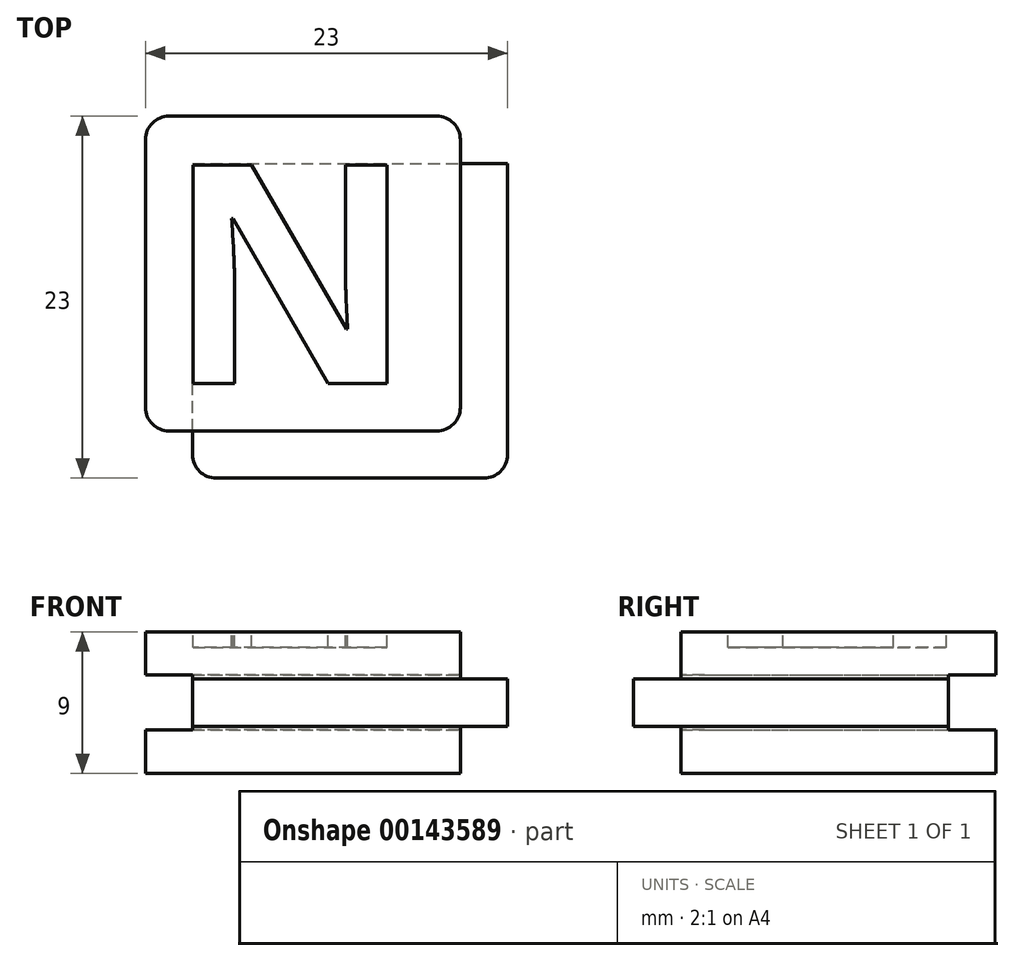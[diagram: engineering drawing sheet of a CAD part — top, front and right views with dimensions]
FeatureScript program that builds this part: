
annotation { "Feature Type Name" : "Feature", "Feature Type Description" : "" }
export const myFeature = defineFeature(function(context is Context, id is Id, definition is map)
    precondition{}
    {
        {
            var Q0;
            Q0=qCreatedBy(makeId("Front.planeOp"),FACE);
            var sketch = newSketch(context, id + "F0", { "sketchPlane" : qUnion([Q0])});
            skLineSegment(sketch, "E0.bottom", {"start": v(10, 4.5) * mm, "end": v(-10, 4.5) * mm});
            skLineSegment(sketch, "E0.top", {"start": v(10, -4.5) * mm, "end": v(-10, -4.5) * mm});
            skLineSegment(sketch, "E0.left", {"start": v(10, 4.5) * mm, "end": v(10, -4.5) * mm});
            skLineSegment(sketch, "E0.right", {"start": v(-10, 4.5) * mm, "end": v(-10, -4.5) * mm});
            skPoint(sketch, "E0.middle", {"position": v(0, 0) * mm});
            skLineSegment(sketch, "E1.bottom", {"start": v(13, 1.5) * mm, "end": v(7, 1.5) * mm});
            skLineSegment(sketch, "E1.top", {"start": v(13, -1.5) * mm, "end": v(7, -1.5) * mm});
            skLineSegment(sketch, "E1.left", {"start": v(13, 1.5) * mm, "end": v(13, -1.5) * mm});
            skLineSegment(sketch, "E1.right", {"start": v(7, 1.5) * mm, "end": v(7, -1.5) * mm});
            skPoint(sketch, "E1.middle", {"position": v(10, 0) * mm});
            skLineSegment(sketch, "E2.bottom", {"start": v(7, 1.5) * mm, "end": v(-7, 1.5) * mm});
            skLineSegment(sketch, "E2.top", {"start": v(7, -1.5) * mm, "end": v(-7, -1.5) * mm});
            skLineSegment(sketch, "E2.right", {"start": v(-7, 1.5) * mm, "end": v(-7, -1.5) * mm});
            skLineSegment(sketch, "E3.bottom", {"start": v(-7, -1.5) * mm, "end": v(-10, -1.5) * mm});
            skLineSegment(sketch, "E3.top", {"start": v(-7, 1.5) * mm, "end": v(-10, 1.5) * mm});
            skLineSegment(sketch, "E3.left", {"start": v(-7, -1.5) * mm, "end": v(-7, 1.5) * mm});
            skLineSegment(sketch, "E3.right", {"start": v(-10, -1.5) * mm, "end": v(-10, 1.5) * mm});
            skSolve(sketch);
        }
        {
            var Q0;
            {var subQ5=sQuery(id+"F0.wireOp",EDGE,"E0.bottom");Q0=makeQuery(id+"F0.imprint","IMPRINT",FACE,{"disambiguationData":[TD([[makeQuery(id+"F0.imprint","IMPRINT",EDGE,{"derivedFrom":subQ5}),1.0]])]});}
            var Q1;
            Q1=makeQuery(id+"F0.imprint","IMPRINT",FACE,{"disambiguationData":[TD([[makeQuery(id+"F0.imprint","IMPRINT",EDGE,{"derivedFrom":sQuery(id+"F0.wireOp",EDGE,"E2.bottom")}),1.0]])]});
            var Q2;
            {var subQ5=sQuery(id+"F0.wireOp",EDGE,"E1.left");Q2=makeQuery(id+"F0.imprint","IMPRINT",FACE,{"disambiguationData":[TD([[makeQuery(id+"F0.imprint","IMPRINT",EDGE,{"derivedFrom":subQ5}),-1.0]])]});}
            var Q3;
            {var subQ5=sQuery(id+"F0.wireOp",EDGE,"E1.right");Q3=makeQuery(id+"F0.imprint","IMPRINT",FACE,{"disambiguationData":[TD([[makeQuery(id+"F0.imprint","IMPRINT",EDGE,{"derivedFrom":subQ5}),1.0]])]});}
            var Q4;
            Q4=makeQuery(id+"F0.imprint","IMPRINT",FACE,{"disambiguationData":[TD([[makeQuery(id+"F0.imprint","IMPRINT",EDGE,{"derivedFrom":sQuery(id+"F0.wireOp",EDGE,"E3.bottom")}),-1.0]])]});
            var Q5;
            {var subQ5=sQuery(id+"F0.wireOp",EDGE,"E0.top");Q5=makeQuery(id+"F0.imprint","IMPRINT",FACE,{"disambiguationData":[TD([[makeQuery(id+"F0.imprint","IMPRINT",EDGE,{"derivedFrom":subQ5}),-1.0]])]});}
            extrude(context, id + "F1", {"entities" : qUnion([Q0, Q1, Q2, Q3, Q4, Q5]), "oppositeDirection" : true, "depth" : 20 * mm});
        }
        {
            var Q0;
            Q0=makeQuery(id+"F0.imprint","IMPRINT",FACE,{"disambiguationData":[TD([[makeQuery(id+"F0.imprint","IMPRINT",EDGE,{"derivedFrom":sQuery(id+"F0.wireOp",EDGE,"E3.bottom")}),-1.0]])]});
            var Q1;
            Q1=makeQuery(id+"F0.imprint","IMPRINT",FACE,{"disambiguationData":[TD([[makeQuery(id+"F0.imprint","IMPRINT",EDGE,{"derivedFrom":sQuery(id+"F0.wireOp",EDGE,"E2.bottom")}),1.0]])]});
            var Q2;
            {var subQ5=sQuery(id+"F0.wireOp",EDGE,"E1.right");Q2=makeQuery(id+"F0.imprint","IMPRINT",FACE,{"disambiguationData":[TD([[makeQuery(id+"F0.imprint","IMPRINT",EDGE,{"derivedFrom":subQ5}),1.0]])]});}
            var Q3;
            {var subQ5=sQuery(id+"F0.wireOp",EDGE,"E1.left");Q3=makeQuery(id+"F0.imprint","IMPRINT",FACE,{"disambiguationData":[TD([[makeQuery(id+"F0.imprint","IMPRINT",EDGE,{"derivedFrom":subQ5}),-1.0]])]});}
            extrude(context, id + "F2", {"entities" : qUnion([Q0, Q1, Q2, Q3]), "operationType" : NewBodyOperationType.ADD, "depth" : 3 * mm});
        }
        {
            var Q0;
            {var subQ0=sQuery(id+"F0.wireOp",EDGE,"E1.left");Q0=makeQuery(id+"F2.boolean.opBoolean","MERGE",FACE,{"derivedFrom":[makeQuery(id+"F1.opExtrude","SWEPT_FACE",FACE,{"disambiguationData":[OSD([subQ0])]}),makeQuery(id+"F2.opExtrude","SWEPT_FACE",FACE,{"disambiguationData":[OSD([subQ0])]})]});}
            var sketch = newSketch(context, id + "F3", { "sketchPlane" : qUnion([Q0])});
            skLineSegment(sketch, "E4.bottom", {"start": v(23, 1.75) * mm, "end": v(17, 1.75) * mm});
            skLineSegment(sketch, "E4.top", {"start": v(23, -1.75) * mm, "end": v(17, -1.75) * mm});
            skLineSegment(sketch, "E4.left", {"start": v(23, 1.75) * mm, "end": v(23, -1.75) * mm});
            skLineSegment(sketch, "E4.right", {"start": v(17, 1.75) * mm, "end": v(17, -1.75) * mm});
            skPoint(sketch, "E4.middle", {"position": v(20, 0) * mm});
            skSolve(sketch);
        }
        {
            var Q0;
            {var subQ1=sQuery(id+"F3.wireOp",EDGE,"E4.bottom");Q0=makeQuery(id+"F3.imprint","IMPRINT",FACE,{"disambiguationData":[TD([[makeQuery(id+"F3.imprint","IMPRINT",EDGE,{"derivedFrom":subQ1}),1.0]])]});}
            var Q1;
            {var subQ1=sQuery(id+"F0.wireOp",EDGE,"E1.left");var subQ8=makeQuery(id+"F1.opExtrude","CAP_EDGE",EDGE,{"disambiguationData":[OSD([subQ1])],"isStart":false});Q1=makeQuery(id+"F3.imprint","IMPRINT",FACE,{"disambiguationData":[TD([[makeQuery(id+"F3.imprint","IMPRINT",EDGE,{"derivedFrom":subQ8}),-1.0]])]});}
            extrude(context, id + "F4", {"entities" : qUnion([Q0, Q1]), "operationType" : NewBodyOperationType.REMOVE, "oppositeDirection" : true, "depth" : 100 * mm});
        }
        {
            var Q0;
            Q0=makeQuery(id+"F4.boolean.opBoolean","COPY",FACE,{"derivedFrom":makeQuery(id+"F4.opExtrude","SWEPT_FACE",FACE,{"disambiguationData":[OSD([sQuery(id+"F3.wireOp",EDGE,"E4.right")])]})});
            var sketch = newSketch(context, id + "F5", { "sketchPlane" : qUnion([Q0])});
            skLineSegment(sketch, "E5.bottom", {"start": v(13, 1.75) * mm, "end": v(7, 1.75) * mm});
            skLineSegment(sketch, "E5.top", {"start": v(13, -1.75) * mm, "end": v(7, -1.75) * mm});
            skLineSegment(sketch, "E5.left", {"start": v(13, 1.75) * mm, "end": v(13, -1.75) * mm});
            skLineSegment(sketch, "E5.right", {"start": v(7, 1.75) * mm, "end": v(7, -1.75) * mm});
            skPoint(sketch, "E5.middle", {"position": v(10, 0) * mm});
            skSolve(sketch);
        }
        {
            var Q0;
            {var subQ3=sQuery(id+"F5.wireOp",EDGE,"E5.left");Q0=makeQuery(id+"F5.imprint","IMPRINT",FACE,{"disambiguationData":[TD([[makeQuery(id+"F5.imprint","IMPRINT",EDGE,{"derivedFrom":subQ3}),-1.0]])]});}
            var Q1;
            {var subQ4=sQuery(id+"F5.wireOp",EDGE,"E5.right");Q1=makeQuery(id+"F5.imprint","IMPRINT",FACE,{"disambiguationData":[TD([[makeQuery(id+"F5.imprint","IMPRINT",EDGE,{"derivedFrom":subQ4}),1.0]])]});}
            extrude(context, id + "F6", {"entities" : qUnion([Q0, Q1]), "operationType" : NewBodyOperationType.REMOVE, "oppositeDirection" : true, "depth" : 100 * mm});
        }
        {
            var Q0;
            Q0=makeQuery(id+"F6.boolean.opBoolean","INTERSECT",EDGE,{"derivedFrom":[makeQuery(id+"F2.opExtrude","CAP_FACE",FACE,{"disambiguationData":[OSD([sQuery(id+"F0.wireOp",EDGE,"E1.bottom"),sQuery(id+"F0.wireOp",EDGE,"E1.top"),sQuery(id+"F0.wireOp",EDGE,"E1.left"),sQuery(id+"F0.wireOp",EDGE,"E2.bottom"),sQuery(id+"F0.wireOp",EDGE,"E2.top"),sQuery(id+"F0.wireOp",EDGE,"E3.bottom"),sQuery(id+"F0.wireOp",EDGE,"E3.top"),sQuery(id+"F0.wireOp",EDGE,"E3.right")])],"isStart":false}),makeQuery(id+"F6.opExtrude","SWEPT_FACE",FACE,{"disambiguationData":[OSD([sQuery(id+"F5.wireOp",EDGE,"E5.right")])]})]});
            var Q1;
            Q1=makeQuery(id+"F2.opExtrude","CAP_EDGE",EDGE,{"disambiguationData":[OSD([sQuery(id+"F0.wireOp",EDGE,"E1.left")])],"isStart":false});
            var Q2;
            {var subQ0=sQuery(id+"F0.wireOp",EDGE,"E0.left");Q2=makeQuery(id+"F1.opExtrude","CAP_EDGE",EDGE,{"disambiguationData":[OSD([subQ0]),TDD([makeQuery(id+"F0.imprint","IMPRINT",EDGE,{"disambiguationData":[TD([[makeQuery(id+"F0.imprint","INTERSECT",VERTEX,{"derivedFrom":[sQuery(id+"F0.wireOp",EDGE,"E0.bottom"),subQ0]}),-1.0]])],"derivedFrom":subQ0})])],"isStart":true});}
            var Q3;
            {var subQ0=sQuery(id+"F0.wireOp",EDGE,"E0.left");Q3=makeQuery(id+"F1.opExtrude","CAP_EDGE",EDGE,{"disambiguationData":[OSD([subQ0]),TDD([makeQuery(id+"F0.imprint","IMPRINT",EDGE,{"disambiguationData":[TD([[makeQuery(id+"F0.imprint","INTERSECT",VERTEX,{"derivedFrom":[sQuery(id+"F0.wireOp",EDGE,"E0.top"),subQ0]}),1.0]])],"derivedFrom":subQ0})])],"isStart":true});}
            var Q4;
            {var subQ0=sQuery(id+"F0.wireOp",EDGE,"E3.right");var subQ1=sQuery(id+"F0.wireOp",EDGE,"E0.right");var subQ3=sQuery(id+"F0.wireOp",EDGE,"E0.top");Q4=makeQuery(id+"F2.boolean.opBoolean","SPLIT",EDGE,{"disambiguationData":[TD([makeQuery(id+"F1.opExtrude","SWEPT_FACE",FACE,{"disambiguationData":[OSD([subQ3])]})])],"derivedFrom":makeQuery(id+"F1.opExtrude","CAP_EDGE",EDGE,{"disambiguationData":[OSD([subQ1,subQ0])],"isStart":true})});}
            var Q5;
            {var subQ1=sQuery(id+"F0.wireOp",EDGE,"E3.right");var subQ2=sQuery(id+"F0.wireOp",EDGE,"E0.right");var subQ3=sQuery(id+"F0.wireOp",EDGE,"E0.bottom");Q5=makeQuery(id+"F2.boolean.opBoolean","SPLIT",EDGE,{"disambiguationData":[TD([makeQuery(id+"F1.opExtrude","SWEPT_FACE",FACE,{"disambiguationData":[OSD([subQ3])]})])],"derivedFrom":makeQuery(id+"F1.opExtrude","CAP_EDGE",EDGE,{"disambiguationData":[OSD([subQ2,subQ1])],"isStart":true})});}
            var Q6;
            Q6=makeQuery(id+"F6.boolean.opBoolean","COPY",EDGE,{"derivedFrom":makeQuery(id+"F6.opExtrude","CAP_EDGE",EDGE,{"disambiguationData":[OSD([sQuery(id+"F5.wireOp",EDGE,"E5.right")])],"isStart":true})});
            var Q7;
            {var subQ0=sQuery(id+"F0.wireOp",EDGE,"E3.right");var subQ1=sQuery(id+"F0.wireOp",EDGE,"E0.right");var subQ2=sQuery(id+"F0.wireOp",EDGE,"E0.bottom");Q7=makeQuery(id+"F4.boolean.opBoolean","SPLIT",EDGE,{"disambiguationData":[TD([makeQuery(id+"F1.opExtrude","SWEPT_FACE",FACE,{"disambiguationData":[OSD([subQ2])]})])],"derivedFrom":makeQuery(id+"F1.opExtrude","CAP_EDGE",EDGE,{"disambiguationData":[OSD([subQ1,subQ0])],"isStart":false})});}
            var Q8;
            {var subQ0=sQuery(id+"F0.wireOp",EDGE,"E3.right");var subQ1=sQuery(id+"F0.wireOp",EDGE,"E0.right");var subQ2=sQuery(id+"F0.wireOp",EDGE,"E0.top");Q8=makeQuery(id+"F4.boolean.opBoolean","SPLIT",EDGE,{"disambiguationData":[TD([makeQuery(id+"F1.opExtrude","SWEPT_FACE",FACE,{"disambiguationData":[OSD([subQ2])]})])],"derivedFrom":makeQuery(id+"F1.opExtrude","CAP_EDGE",EDGE,{"disambiguationData":[OSD([subQ1,subQ0])],"isStart":false})});}
            var Q9;
            Q9=makeQuery(id+"F4.boolean.opBoolean","COPY",EDGE,{"derivedFrom":makeQuery(id+"F4.opExtrude","CAP_EDGE",EDGE,{"disambiguationData":[OSD([sQuery(id+"F3.wireOp",EDGE,"E4.right")])],"isStart":true})});
            var Q10;
            {var subQ0=sQuery(id+"F0.wireOp",EDGE,"E0.left");Q10=makeQuery(id+"F1.opExtrude","CAP_EDGE",EDGE,{"disambiguationData":[OSD([subQ0]),TDD([makeQuery(id+"F0.imprint","IMPRINT",EDGE,{"disambiguationData":[TD([[makeQuery(id+"F0.imprint","INTERSECT",VERTEX,{"derivedFrom":[sQuery(id+"F0.wireOp",EDGE,"E0.bottom"),subQ0]}),-1.0]])],"derivedFrom":subQ0})])],"isStart":false});}
            var Q11;
            {var subQ0=sQuery(id+"F0.wireOp",EDGE,"E0.left");Q11=makeQuery(id+"F1.opExtrude","CAP_EDGE",EDGE,{"disambiguationData":[OSD([subQ0]),TDD([makeQuery(id+"F0.imprint","IMPRINT",EDGE,{"disambiguationData":[TD([[makeQuery(id+"F0.imprint","INTERSECT",VERTEX,{"derivedFrom":[sQuery(id+"F0.wireOp",EDGE,"E0.top"),subQ0]}),1.0]])],"derivedFrom":subQ0})])],"isStart":false});}
            fillet(context, id + "F7", {"entities" : qUnion([Q0, Q1, Q2, Q3, Q4, Q5, Q6, Q7, Q8, Q9, Q10, Q11]), "radius" : 1.5 * mm, "tangentPropagation" : true, "allowEdgeOverflow" : false});
        }
        {
            var Q0;
            Q0=makeQuery(id+"F1.opExtrude","SWEPT_FACE",FACE,{"disambiguationData":[OSD([sQuery(id+"F0.wireOp",EDGE,"E0.bottom")])]});
            var sketch = newSketch(context, id + "F8", { "sketchPlane" : qUnion([Q0])});
            skText(sketch, "E6", { "text": "N", "fontName": "OpenSans-Bold.ttf"});
            skLineSegment(sketch, "E7.0", {"start": v(8.95, 3) * mm, "end": v(-11.07, 3) * mm});
            const initialGuessF8  = {"E6": [-0.00872, 0.003, 1, 0, 0.014]};
            skSetInitialGuess(sketch, initialGuessF8);
            skSolve(sketch);
        }
        {
            var Q0;
            {var subQ0=sQuery(id+"F8.wireOp",EDGE,"E6.sketch_text.stroke-1");Q0=makeQuery(id+"F8.imprint","IMPRINT",FACE,{"disambiguationData":[TD([[makeQuery(id+"F8.imprint","IMPRINT",EDGE,{"derivedFrom":subQ0}),-1.0]])]});}
            extrude(context, id + "F9", {"entities" : qUnion([Q0]), "operationType" : NewBodyOperationType.REMOVE, "oppositeDirection" : true, "depth" : 1 * mm});
        }
    });
